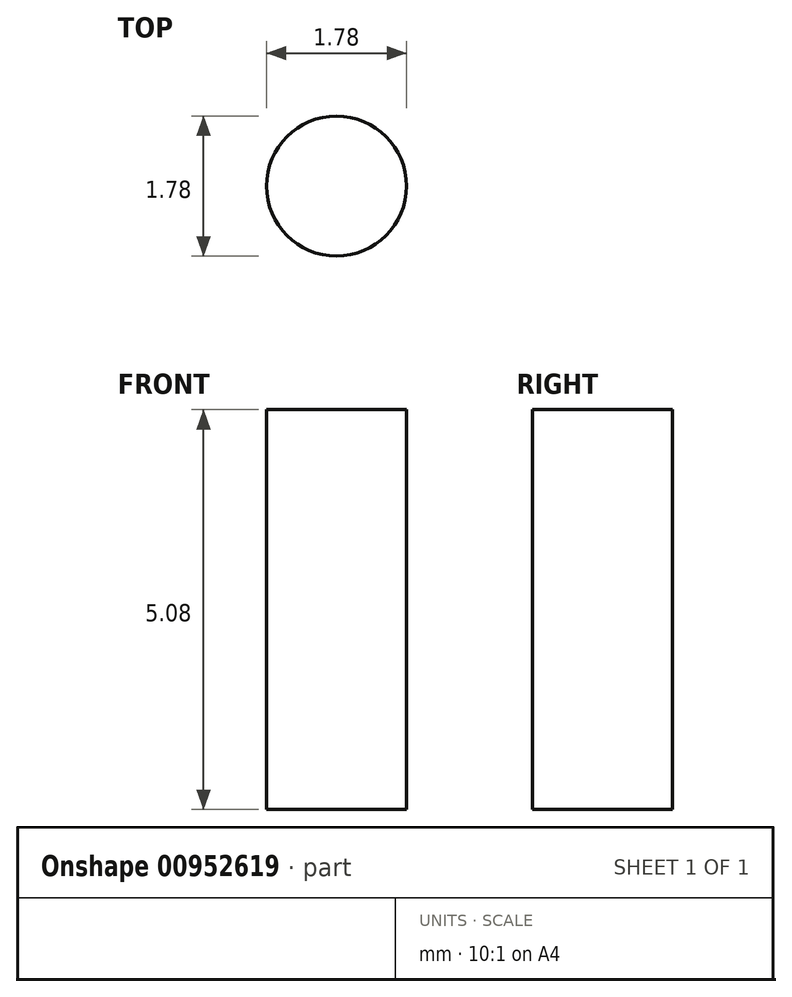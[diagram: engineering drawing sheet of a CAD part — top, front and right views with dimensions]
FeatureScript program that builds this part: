
annotation { "Feature Type Name" : "Feature", "Feature Type Description" : "" }
export const myFeature = defineFeature(function(context is Context, id is Id, definition is map)
    precondition{}
    {
        {
            var Q0;
            Q0=qCreatedBy(makeId("Top.planeOp"),FACE);
            var sketch = newSketch(context, id + "F0", { "sketchPlane" : qUnion([Q0])});
            skCircle(sketch, "E0", {"center": v(0, 0) * mm, "radius": 0.89 * mm});
            skSolve(sketch);
        }
        {
            var Q0;
            Q0 = qSketchRegion(id + "F0", true);
            extrude(context, id + "F1", {"entities" : qUnion([Q0]), "depth" : 5.08 * mm, "offsetDistance" : 25.4 * mm});
        }
    });
